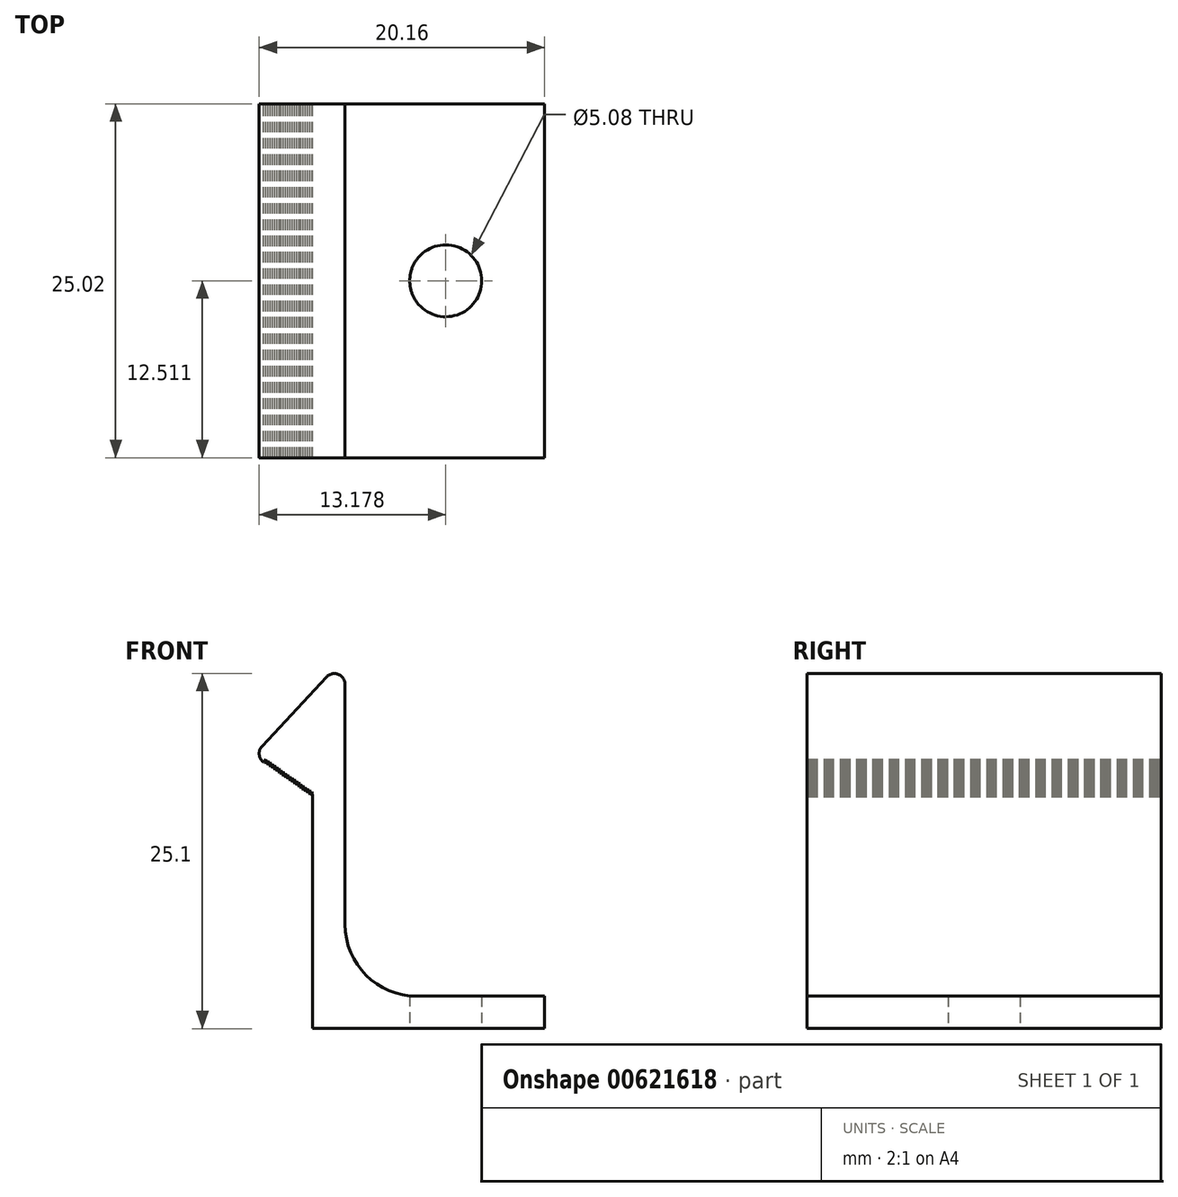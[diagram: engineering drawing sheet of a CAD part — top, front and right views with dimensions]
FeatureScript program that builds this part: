
annotation { "Feature Type Name" : "Feature", "Feature Type Description" : "" }
export const myFeature = defineFeature(function(context is Context, id is Id, definition is map)
    precondition{}
    {
        {
            var Q0;
            Q0=qCreatedBy(makeId("Front.planeOp"),FACE);
            var sketch = newSketch(context, id + "F0", { "sketchPlane" : qUnion([Q0])});
            skLineSegment(sketch, "E0", {"start": v(0, -8.86) * mm, "end": v(0, 7.53) * mm});
            skLineSegment(sketch, "E1", {"start": v(0, -8.86) * mm, "end": v(16.38, -8.86) * mm});
            skLineSegment(sketch, "E2", {"start": v(16.38, -8.86) * mm, "end": v(16.38, -6.57) * mm});
            skLineSegment(sketch, "E3", {"start": v(-3.58, 11.11) * mm, "end": v(0.97, 16) * mm});
            skLineSegment(sketch, "E4", {"start": v(2.29, 15.47) * mm, "end": v(2.29, -1.49) * mm});
            skLineSegment(sketch, "E5", {"start": v(7.37, -6.57) * mm, "end": v(16.38, -6.57) * mm});
            skPoint(sketch, "E6.visualSharp", {"position": v(2.29, 17.4) * mm});
            skArc(sketch, "E6.filletArc", {"start": v(2.29, 15.47) * mm, "mid": v(1.8, 16.18) * mm, "end": v(0.97, 16) * mm});
            skArc(sketch, "E7.filletArc", {"start": v(-3.58, 11.11) * mm, "mid": v(-3.78, 10.52) * mm, "end": v(-3.46, 9.97) * mm});
            skLineSegment(sketch, "E8", {"start": v(-3.46, 9.97) * mm, "end": v(-3.3, 10.2) * mm});
            skLineSegment(sketch, "E9", {"start": v(-3.3, 10.2) * mm, "end": v(-3.3, 9.86) * mm});
            skLineSegment(sketch, "E10", {"start": v(-3.15, 10.08) * mm, "end": v(-3.3, 9.86) * mm});
            skLineSegment(sketch, "E11", {"start": v(-3.15, 10.08) * mm, "end": v(-3.15, 9.75) * mm});
            skLineSegment(sketch, "E12", {"start": v(-3.15, 9.75) * mm, "end": v(-3, 9.97) * mm});
            skLineSegment(sketch, "E13", {"start": v(-3, 9.97) * mm, "end": v(-3, 9.64) * mm});
            skLineSegment(sketch, "E14", {"start": v(-3, 9.64) * mm, "end": v(-2.84, 9.86) * mm});
            skLineSegment(sketch, "E15", {"start": v(-2.84, 9.86) * mm, "end": v(-2.84, 9.53) * mm});
            skLineSegment(sketch, "E16", {"start": v(-2.84, 9.53) * mm, "end": v(-2.68, 9.75) * mm});
            skLineSegment(sketch, "E17", {"start": v(-2.68, 9.75) * mm, "end": v(-2.68, 9.42) * mm});
            skLineSegment(sketch, "E18", {"start": v(-2.68, 9.42) * mm, "end": v(-2.53, 9.64) * mm});
            skLineSegment(sketch, "E19", {"start": v(-2.53, 9.64) * mm, "end": v(-2.53, 9.31) * mm});
            skLineSegment(sketch, "E20", {"start": v(-2.53, 9.31) * mm, "end": v(-2.37, 9.53) * mm});
            skLineSegment(sketch, "E21", {"start": v(-2.37, 9.53) * mm, "end": v(-2.37, 9.2) * mm});
            skLineSegment(sketch, "E22", {"start": v(-2.37, 9.2) * mm, "end": v(-2.22, 9.42) * mm});
            skLineSegment(sketch, "E23", {"start": v(-2.22, 9.42) * mm, "end": v(-2.22, 9.1) * mm});
            skLineSegment(sketch, "E24", {"start": v(-2.22, 9.1) * mm, "end": v(-2.06, 9.31) * mm});
            skLineSegment(sketch, "E25", {"start": v(-2.06, 9.31) * mm, "end": v(-2.06, 8.98) * mm});
            skLineSegment(sketch, "E26", {"start": v(-2.06, 8.98) * mm, "end": v(-1.9, 9.2) * mm});
            skLineSegment(sketch, "E27", {"start": v(-1.9, 9.2) * mm, "end": v(-1.9, 8.88) * mm});
            skLineSegment(sketch, "E28", {"start": v(-1.9, 8.88) * mm, "end": v(-1.75, 9.1) * mm});
            skLineSegment(sketch, "E29", {"start": v(-1.75, 9.1) * mm, "end": v(-1.75, 8.77) * mm});
            skLineSegment(sketch, "E30", {"start": v(-1.75, 8.77) * mm, "end": v(-1.6, 8.98) * mm});
            skLineSegment(sketch, "E31", {"start": v(-1.6, 8.98) * mm, "end": v(-1.6, 8.66) * mm});
            skLineSegment(sketch, "E32", {"start": v(-1.6, 8.66) * mm, "end": v(-1.44, 8.88) * mm});
            skLineSegment(sketch, "E33", {"start": v(-1.44, 8.88) * mm, "end": v(-1.44, 8.55) * mm});
            skLineSegment(sketch, "E34", {"start": v(-1.44, 8.55) * mm, "end": v(-1.29, 8.77) * mm});
            skLineSegment(sketch, "E35", {"start": v(-1.29, 8.77) * mm, "end": v(-1.29, 8.44) * mm});
            skLineSegment(sketch, "E36", {"start": v(-1.29, 8.44) * mm, "end": v(-1.13, 8.66) * mm});
            skLineSegment(sketch, "E37", {"start": v(-1.13, 8.66) * mm, "end": v(-1.13, 8.33) * mm});
            skLineSegment(sketch, "E38", {"start": v(-1.13, 8.33) * mm, "end": v(-0.97, 8.55) * mm});
            skLineSegment(sketch, "E39", {"start": v(-0.97, 8.55) * mm, "end": v(-0.97, 8.22) * mm});
            skLineSegment(sketch, "E40", {"start": v(-0.97, 8.22) * mm, "end": v(-0.82, 8.44) * mm});
            skLineSegment(sketch, "E41", {"start": v(-0.82, 8.44) * mm, "end": v(-0.82, 8.1) * mm});
            skLineSegment(sketch, "E42", {"start": v(-0.52, 8.22) * mm, "end": v(-0.52, 7.9) * mm});
            skLineSegment(sketch, "E43", {"start": v(-0.52, 7.9) * mm, "end": v(-0.36, 8.11) * mm});
            skLineSegment(sketch, "E44", {"start": v(-0.36, 8.11) * mm, "end": v(-0.36, 7.78) * mm});
            skLineSegment(sketch, "E45", {"start": v(-0.82, 8.1) * mm, "end": v(-0.66, 8.33) * mm});
            skLineSegment(sketch, "E46", {"start": v(-0.66, 8.33) * mm, "end": v(-0.66, 8) * mm});
            skLineSegment(sketch, "E47", {"start": v(-0.66, 8) * mm, "end": v(-0.52, 8.22) * mm});
            skLineSegment(sketch, "E48", {"start": v(-0.36, 7.78) * mm, "end": v(-0.2, 8) * mm});
            skLineSegment(sketch, "E49", {"start": v(-0.2, 8) * mm, "end": v(-0.2, 7.67) * mm});
            skLineSegment(sketch, "E50", {"start": v(-0.2, 7.67) * mm, "end": v(-0.05, 7.9) * mm});
            skLineSegment(sketch, "E51", {"start": v(-0.05, 7.9) * mm, "end": v(0, 7.53) * mm});
            skArc(sketch, "E52.filletArc", {"start": v(2.29, -1.49) * mm, "mid": v(3.77, -5.08) * mm, "end": v(7.37, -6.57) * mm});
            skSolve(sketch);
        }
        {
            var Q0;
            Q0 = qSketchRegion(id + "F0", true);
            extrude(context, id + "F1", {"entities" : qUnion([Q0]), "depth" : 25.02 * mm, "offsetDistance" : 25.4 * mm});
        }
        {
            var Q0;
            Q0=makeQuery(id+"F1.opExtrude","SWEPT_FACE",FACE,{"disambiguationData":[OSD([sQuery(id+"F0.wireOp",EDGE,"E1")])]});
            var sketch = newSketch(context, id + "F2", { "sketchPlane" : qUnion([Q0])});
            skPoint(sketch, "E53.endSnap0", {"position": v(16.38, 12.5) * mm});
            skCircle(sketch, "E54", {"center": v(9.4, 12.5) * mm, "radius": 2.41 * mm});
            skSolve(sketch);
        }
        {
            var Q0;
            Q0=sQuery(id+"F2.wireOp",VERTEX,"E54.center");
            var Q1;
            Q1=makeQuery(id+"F1.opExtrude","SWEPT_BODY",BODY,{"disambiguationData":[OSD([sQuery(id+"F0.wireOp",EDGE,"E0"),sQuery(id+"F0.wireOp",EDGE,"E1"),sQuery(id+"F0.wireOp",EDGE,"E2"),sQuery(id+"F0.wireOp",EDGE,"E3"),sQuery(id+"F0.wireOp",EDGE,"E4"),sQuery(id+"F0.wireOp",EDGE,"E5"),sQuery(id+"F0.wireOp",EDGE,"E6.filletArc"),sQuery(id+"F0.wireOp",EDGE,"E7.filletArc"),sQuery(id+"F0.wireOp",EDGE,"E8"),sQuery(id+"F0.wireOp",EDGE,"E9"),sQuery(id+"F0.wireOp",EDGE,"E10"),sQuery(id+"F0.wireOp",EDGE,"E11"),sQuery(id+"F0.wireOp",EDGE,"E12"),sQuery(id+"F0.wireOp",EDGE,"E13"),sQuery(id+"F0.wireOp",EDGE,"E14"),sQuery(id+"F0.wireOp",EDGE,"E15"),sQuery(id+"F0.wireOp",EDGE,"E16"),sQuery(id+"F0.wireOp",EDGE,"E17"),sQuery(id+"F0.wireOp",EDGE,"E18"),sQuery(id+"F0.wireOp",EDGE,"E19"),sQuery(id+"F0.wireOp",EDGE,"E20"),sQuery(id+"F0.wireOp",EDGE,"E21"),sQuery(id+"F0.wireOp",EDGE,"E22"),sQuery(id+"F0.wireOp",EDGE,"E23"),sQuery(id+"F0.wireOp",EDGE,"E24"),sQuery(id+"F0.wireOp",EDGE,"E25"),sQuery(id+"F0.wireOp",EDGE,"E26"),sQuery(id+"F0.wireOp",EDGE,"E27"),sQuery(id+"F0.wireOp",EDGE,"E28"),sQuery(id+"F0.wireOp",EDGE,"E29"),sQuery(id+"F0.wireOp",EDGE,"E30"),sQuery(id+"F0.wireOp",EDGE,"E31"),sQuery(id+"F0.wireOp",EDGE,"E32"),sQuery(id+"F0.wireOp",EDGE,"E33"),sQuery(id+"F0.wireOp",EDGE,"E34"),sQuery(id+"F0.wireOp",EDGE,"E35"),sQuery(id+"F0.wireOp",EDGE,"E36"),sQuery(id+"F0.wireOp",EDGE,"E37"),sQuery(id+"F0.wireOp",EDGE,"E38"),sQuery(id+"F0.wireOp",EDGE,"E39"),sQuery(id+"F0.wireOp",EDGE,"E40"),sQuery(id+"F0.wireOp",EDGE,"E41"),sQuery(id+"F0.wireOp",EDGE,"E42"),sQuery(id+"F0.wireOp",EDGE,"E43"),sQuery(id+"F0.wireOp",EDGE,"E44"),sQuery(id+"F0.wireOp",EDGE,"E45"),sQuery(id+"F0.wireOp",EDGE,"E46"),sQuery(id+"F0.wireOp",EDGE,"E47"),sQuery(id+"F0.wireOp",EDGE,"E48"),sQuery(id+"F0.wireOp",EDGE,"E49"),sQuery(id+"F0.wireOp",EDGE,"E50"),sQuery(id+"F0.wireOp",EDGE,"E51"),sQuery(id+"F0.wireOp",EDGE,"E52.filletArc")])]});
            hole(context, id + "F3", {"style" : HoleStyle.SIMPLE, "endStyle" : HoleEndStyle.THROUGH, "holeDiameter" : 5.08 * mm, "majorDiameter" : 6.35 * mm, "isTappedThrough" : true, "tappedDepth" : 12.7 * mm, "tapClearance" : 3, "locations" : qUnion([Q0]), "scope" : qUnion([Q1])});
        }
    });
